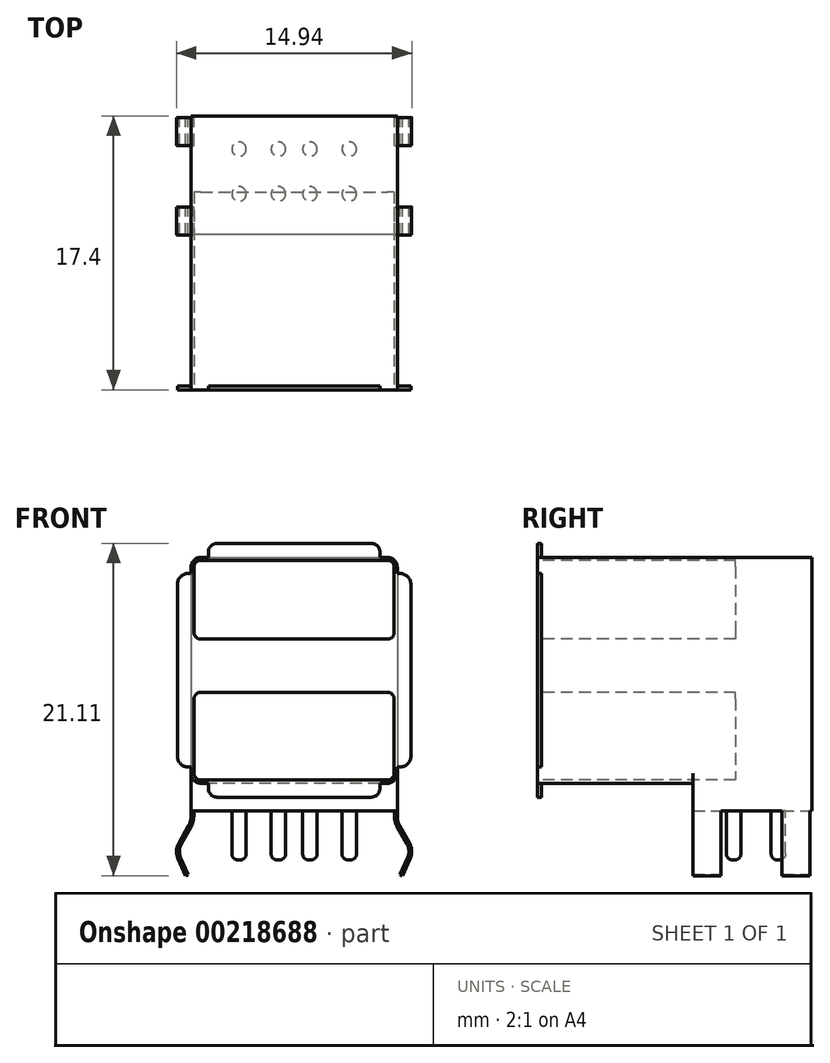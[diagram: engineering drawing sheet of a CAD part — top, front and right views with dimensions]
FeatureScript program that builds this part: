
annotation { "Feature Type Name" : "Feature", "Feature Type Description" : "" }
export const myFeature = defineFeature(function(context is Context, id is Id, definition is map)
    precondition{}
    {
        {
            var Q0;
            Q0=qCreatedBy(makeId("Top.planeOp"),FACE);
            var sketch = newSketch(context, id + "F0", { "sketchPlane" : qUnion([Q0])});
            skLineSegment(sketch, "E0.bottom", {"start": v(-6.55, 8.7) * mm, "end": v(6.55, 8.7) * mm});
            skLineSegment(sketch, "E0.top", {"start": v(-6.55, -8.7) * mm, "end": v(6.55, -8.7) * mm});
            skLineSegment(sketch, "E0.left", {"start": v(-6.55, 8.7) * mm, "end": v(-6.55, -8.7) * mm});
            skLineSegment(sketch, "E0.right", {"start": v(6.55, 8.7) * mm, "end": v(6.55, -8.7) * mm});
            skLineSegment(sketch, "E1", {"start": v(0, 8.7) * mm, "end": v(0, -8.7) * mm, "construction": true});
            skLineSegment(sketch, "E2", {"start": v(-6.55, 0) * mm, "end": v(6.55, 0) * mm, "construction": true});
            skSolve(sketch);
        }
        {
            var Q0;
            Q0 = qSketchRegion(id + "F0", true);
            extrude(context, id + "F1", {"entities" : qUnion([Q0]), "depth" : 14.35 * mm});
        }
        {
            var Q0;
            Q0=makeQuery(id+"F1.opExtrude","CAP_FACE",FACE,{"disambiguationData":[OSD([sQuery(id+"F0.wireOp",EDGE,"E0.bottom"),sQuery(id+"F0.wireOp",EDGE,"E0.top"),sQuery(id+"F0.wireOp",EDGE,"E0.left"),sQuery(id+"F0.wireOp",EDGE,"E0.right")])],"isStart":true});
            var sketch = newSketch(context, id + "F2", { "sketchPlane" : qUnion([Q0])});
            skLineSegment(sketch, "E3.bottom", {"start": v(6.55, -8.7) * mm, "end": v(-6.55, -8.7) * mm});
            skLineSegment(sketch, "E3.top", {"start": v(6.55, -1.16) * mm, "end": v(-6.55, -1.16) * mm});
            skLineSegment(sketch, "E3.left", {"start": v(6.55, -8.7) * mm, "end": v(6.55, -1.16) * mm});
            skLineSegment(sketch, "E3.right", {"start": v(-6.55, -8.7) * mm, "end": v(-6.55, -1.16) * mm});
            skSolve(sketch);
        }
        {
            var Q0;
            Q0 = qSketchRegion(id + "F2", true);
            extrude(context, id + "F3", {"entities" : qUnion([Q0]), "operationType" : NewBodyOperationType.ADD, "depth" : 16.12 * mm - 14.35 * mm});
        }
        {
            var Q0;
            Q0=qCreatedBy(makeId("Front.planeOp"),FACE);
            cPlane(context, id + "F4", {"entities" : qUnion([Q0]), "cplaneType" : CPlaneType.OFFSET, "offset" : 2.03 * mm, "oppositeDirection" : true, "width" : 152.4 * mm, "height" : 152.4 * mm});
        }
        {
            var Q0;
            Q0=qCreatedBy(id+"F4.planeOp",FACE);
            cPlane(context, id + "F5", {"entities" : qUnion([Q0]), "cplaneType" : CPlaneType.OFFSET, "offset" : 5.68 * mm, "oppositeDirection" : true, "width" : 152.4 * mm, "height" : 152.4 * mm});
        }
        {
            var Q0;
            Q0=qCreatedBy(id+"F4.planeOp",FACE);
            var sketch = newSketch(context, id + "F6", { "sketchPlane" : qUnion([Q0])});
            skLineSegment(sketch, "E4", {"start": v(6.55, -1.77) * mm, "end": v(6.55, -2.12) * mm});
            skLineSegment(sketch, "E5", {"start": v(6.7, -2.67) * mm, "end": v(7.32, -3.79) * mm});
            skLineSegment(sketch, "E6", {"start": v(7.37, -4.81) * mm, "end": v(6.88, -5.87) * mm});
            skPoint(sketch, "E7.visualSharp", {"position": v(7.6, -4.29) * mm});
            skArc(sketch, "E7.filletArc", {"start": v(7.37, -4.81) * mm, "mid": v(7.47, -4.3) * mm, "end": v(7.32, -3.79) * mm});
            skPoint(sketch, "E8.visualSharp", {"position": v(6.55, -2.41) * mm});
            skArc(sketch, "E8.filletArc", {"start": v(6.55, -2.12) * mm, "mid": v(6.59, -2.4) * mm, "end": v(6.7, -2.67) * mm});
            skLineSegment(sketch, "E9.0", {"start": v(7.2, -4.74) * mm, "end": v(6.72, -5.8) * mm});
            skLineSegment(sketch, "E9.1", {"start": v(6.37, -1.77) * mm, "end": v(6.37, -2.12) * mm});
            skArc(sketch, "E9.2", {"start": v(6.37, -2.12) * mm, "mid": v(6.41, -2.45) * mm, "end": v(6.54, -2.76) * mm});
            skLineSegment(sketch, "E9.3", {"start": v(6.54, -2.76) * mm, "end": v(7.17, -3.88) * mm});
            skArc(sketch, "E9.4", {"start": v(7.2, -4.74) * mm, "mid": v(7.3, -4.3) * mm, "end": v(7.17, -3.88) * mm});
            skLineSegment(sketch, "E10", {"start": v(6.72, -5.8) * mm, "end": v(6.88, -5.87) * mm});
            skLineSegment(sketch, "E11", {"start": v(6.37, -1.77) * mm, "end": v(6.55, -1.77) * mm});
            skLineSegment(sketch, "E12.MirrorCS", {"start": v(-6.37, -1.77) * mm, "end": v(-6.55, -1.77) * mm});
            skLineSegment(sketch, "E13.MirrorCS", {"start": v(-6.72, -5.8) * mm, "end": v(-6.88, -5.87) * mm});
            skLineSegment(sketch, "E14.MirrorCS", {"start": v(-6.55, -1.77) * mm, "end": v(-6.55, -2.12) * mm});
            skLineSegment(sketch, "E15.MirrorCS", {"start": v(-6.37, -1.77) * mm, "end": v(-6.37, -2.12) * mm});
            skArc(sketch, "E16.MirrorCS", {"start": v(-7.2, -4.74) * mm, "mid": v(-7.3, -4.3) * mm, "end": v(-7.17, -3.88) * mm});
            skLineSegment(sketch, "E17.MirrorCS", {"start": v(-6.54, -2.76) * mm, "end": v(-7.17, -3.88) * mm});
            skArc(sketch, "E18.MirrorCS", {"start": v(-6.37, -2.12) * mm, "mid": v(-6.41, -2.45) * mm, "end": v(-6.54, -2.76) * mm});
            skArc(sketch, "E19.MirrorCS", {"start": v(-7.37, -4.81) * mm, "mid": v(-7.47, -4.3) * mm, "end": v(-7.32, -3.79) * mm});
            skLineSegment(sketch, "E20.MirrorCS", {"start": v(-6.7, -2.67) * mm, "end": v(-7.32, -3.79) * mm});
            skArc(sketch, "E21.MirrorCS", {"start": v(-6.55, -2.12) * mm, "mid": v(-6.59, -2.4) * mm, "end": v(-6.7, -2.67) * mm});
            skPoint(sketch, "E22.MirrorP", {"position": v(-7.6, -4.29) * mm});
            skPoint(sketch, "E23.MirrorP", {"position": v(-6.55, -2.41) * mm});
            skLineSegment(sketch, "E24.MirrorCS", {"start": v(-7.37, -4.81) * mm, "end": v(-6.88, -5.87) * mm});
            skLineSegment(sketch, "E25.MirrorCS", {"start": v(-7.2, -4.74) * mm, "end": v(-6.72, -5.8) * mm});
            skSolve(sketch);
        }
        {
            var Q0;
            Q0 = qSketchRegion(id + "F6", true);
            extrude(context, id + "F7", {"entities" : qUnion([Q0]), "operationType" : NewBodyOperationType.ADD, "endBound" : BoundingType.SYMMETRIC, "depth" : 1.78 * mm});
        }
        {
            var Q0;
            Q0=qCreatedBy(id+"F5.planeOp",FACE);
            var sketch = newSketch(context, id + "F8", { "sketchPlane" : qUnion([Q0])});
            skLineSegment(sketch, "E26.0", {"start": v(6.37, -1.77) * mm, "end": v(6.37, -2.12) * mm});
            skLineSegment(sketch, "E26.1", {"start": v(6.55, -1.77) * mm, "end": v(6.55, -2.12) * mm});
            skArc(sketch, "E26.2", {"start": v(6.37, -2.12) * mm, "mid": v(6.41, -2.45) * mm, "end": v(6.54, -2.76) * mm});
            skArc(sketch, "E26.3", {"start": v(6.55, -2.12) * mm, "mid": v(6.59, -2.4) * mm, "end": v(6.7, -2.67) * mm});
            skLineSegment(sketch, "E26.4", {"start": v(6.54, -2.76) * mm, "end": v(7.17, -3.88) * mm});
            skLineSegment(sketch, "E26.5", {"start": v(6.7, -2.67) * mm, "end": v(7.32, -3.79) * mm});
            skArc(sketch, "E26.6", {"start": v(7.2, -4.74) * mm, "mid": v(7.3, -4.3) * mm, "end": v(7.17, -3.88) * mm});
            skArc(sketch, "E26.7", {"start": v(7.37, -4.81) * mm, "mid": v(7.47, -4.3) * mm, "end": v(7.32, -3.79) * mm});
            skLineSegment(sketch, "E26.8", {"start": v(6.72, -5.8) * mm, "end": v(6.88, -5.87) * mm});
            skLineSegment(sketch, "E26.9", {"start": v(7.2, -4.74) * mm, "end": v(6.72, -5.8) * mm});
            skLineSegment(sketch, "E26.10", {"start": v(7.37, -4.81) * mm, "end": v(6.88, -5.87) * mm});
            skLineSegment(sketch, "E26.11", {"start": v(-7.37, -4.81) * mm, "end": v(-6.88, -5.87) * mm});
            skArc(sketch, "E26.12", {"start": v(-7.37, -4.81) * mm, "mid": v(-7.47, -4.3) * mm, "end": v(-7.32, -3.79) * mm});
            skLineSegment(sketch, "E26.13", {"start": v(-6.7, -2.67) * mm, "end": v(-7.32, -3.79) * mm});
            skArc(sketch, "E26.14", {"start": v(-6.55, -2.12) * mm, "mid": v(-6.59, -2.4) * mm, "end": v(-6.7, -2.67) * mm});
            skLineSegment(sketch, "E26.15", {"start": v(-6.55, -1.77) * mm, "end": v(-6.55, -2.12) * mm});
            skLineSegment(sketch, "E26.16", {"start": v(-6.37, -1.77) * mm, "end": v(-6.37, -2.12) * mm});
            skArc(sketch, "E26.17", {"start": v(-6.37, -2.12) * mm, "mid": v(-6.41, -2.45) * mm, "end": v(-6.54, -2.76) * mm});
            skLineSegment(sketch, "E26.18", {"start": v(-6.54, -2.76) * mm, "end": v(-7.17, -3.88) * mm});
            skArc(sketch, "E26.19", {"start": v(-7.2, -4.74) * mm, "mid": v(-7.3, -4.3) * mm, "end": v(-7.17, -3.88) * mm});
            skLineSegment(sketch, "E26.20", {"start": v(-7.2, -4.74) * mm, "end": v(-6.72, -5.8) * mm});
            skLineSegment(sketch, "E26.21", {"start": v(-6.72, -5.8) * mm, "end": v(-6.88, -5.87) * mm});
            skLineSegment(sketch, "E27", {"start": v(-6.55, -1.77) * mm, "end": v(-6.37, -1.77) * mm});
            skLineSegment(sketch, "E28", {"start": v(6.37, -1.77) * mm, "end": v(6.55, -1.77) * mm});
            skSolve(sketch);
        }
        {
            var Q0;
            Q0=makeQuery(id+"F8.imprint","IMPRINT",FACE,{"disambiguationData":[TD([[makeQuery(id+"F8.imprint","IMPRINT",EDGE,{"derivedFrom":sQuery(id+"F8.wireOp",EDGE,"E26.11")}),1.0]])]});
            var Q1;
            Q1=makeQuery(id+"F8.imprint","IMPRINT",FACE,{"disambiguationData":[TD([[makeQuery(id+"F8.imprint","IMPRINT",EDGE,{"derivedFrom":sQuery(id+"F8.wireOp",EDGE,"E26.0")}),1.0]])]});
            extrude(context, id + "F9", {"entities" : qUnion([Q0, Q1]), "operationType" : NewBodyOperationType.ADD, "endBound" : BoundingType.SYMMETRIC, "depth" : 1.78 * mm});
        }
        {
            var Q0;
            Q0=makeQuery(id+"F3.opExtrude","CAP_FACE",FACE,{"disambiguationData":[OSD([sQuery(id+"F2.wireOp",EDGE,"E3.bottom"),sQuery(id+"F2.wireOp",EDGE,"E3.top"),sQuery(id+"F2.wireOp",EDGE,"E3.left"),sQuery(id+"F2.wireOp",EDGE,"E3.right")])],"isStart":false});
            var sketch = newSketch(context, id + "F10", { "sketchPlane" : qUnion([Q0])});
            skCircle(sketch, "E29", {"center": v(3.5, -6.59) * mm, "radius": 0.46 * mm});
            skCircle(sketch, "E30", {"center": v(1, -6.59) * mm, "radius": 0.46 * mm});
            skCircle(sketch, "E31", {"center": v(-1, -6.59) * mm, "radius": 0.46 * mm});
            skCircle(sketch, "E32", {"center": v(-3.5, -6.59) * mm, "radius": 0.46 * mm});
            skCircle(sketch, "E33", {"center": v(3.5, -3.74) * mm, "radius": 0.46 * mm});
            skCircle(sketch, "E34", {"center": v(1, -3.74) * mm, "radius": 0.46 * mm});
            skCircle(sketch, "E35", {"center": v(-1, -3.74) * mm, "radius": 0.46 * mm});
            skCircle(sketch, "E36", {"center": v(-3.5, -3.74) * mm, "radius": 0.46 * mm});
            skSolve(sketch);
        }
        {
            var Q0;
            Q0 = qSketchRegion(id + "F10", true);
            extrude(context, id + "F11", {"entities" : qUnion([Q0]), "operationType" : NewBodyOperationType.ADD, "depth" : 3.1 * mm});
        }
        {
            var Q0;
            Q0=makeQuery(id+"F11.opExtrude","CAP_EDGE",EDGE,{"disambiguationData":[OSD([sQuery(id+"F10.wireOp",EDGE,"E29")])],"isStart":false});
            var Q1;
            Q1=makeQuery(id+"F11.opExtrude","CAP_EDGE",EDGE,{"disambiguationData":[OSD([sQuery(id+"F10.wireOp",EDGE,"E30")])],"isStart":false});
            var Q2;
            Q2=makeQuery(id+"F11.opExtrude","CAP_EDGE",EDGE,{"disambiguationData":[OSD([sQuery(id+"F10.wireOp",EDGE,"E31")])],"isStart":false});
            var Q3;
            Q3=makeQuery(id+"F11.opExtrude","CAP_EDGE",EDGE,{"disambiguationData":[OSD([sQuery(id+"F10.wireOp",EDGE,"E32")])],"isStart":false});
            var Q4;
            Q4=makeQuery(id+"F11.opExtrude","CAP_EDGE",EDGE,{"disambiguationData":[OSD([sQuery(id+"F10.wireOp",EDGE,"E33")])],"isStart":false});
            var Q5;
            Q5=makeQuery(id+"F11.opExtrude","CAP_EDGE",EDGE,{"disambiguationData":[OSD([sQuery(id+"F10.wireOp",EDGE,"E34")])],"isStart":false});
            var Q6;
            Q6=makeQuery(id+"F11.opExtrude","CAP_EDGE",EDGE,{"disambiguationData":[OSD([sQuery(id+"F10.wireOp",EDGE,"E35")])],"isStart":false});
            var Q7;
            Q7=makeQuery(id+"F11.opExtrude","CAP_EDGE",EDGE,{"disambiguationData":[OSD([sQuery(id+"F10.wireOp",EDGE,"E36")])],"isStart":false});
            fillet(context, id + "F12", {"entities" : qUnion([Q0, Q1, Q2, Q3, Q4, Q5, Q6, Q7]), "radius" : 0.38 * mm, "tangentPropagation" : true, "allowEdgeOverflow" : false});
        }
        {
            var Q0;
            Q0=makeQuery(id+"F1.opExtrude","SWEPT_FACE",FACE,{"disambiguationData":[OSD([sQuery(id+"F0.wireOp",EDGE,"E0.top")])]});
            var sketch = newSketch(context, id + "F13", { "sketchPlane" : qUnion([Q0])});
            skLineSegment(sketch, "E37.bottom", {"start": v(-4.9, 15.24) * mm, "end": v(4.9, 15.24) * mm});
            skLineSegment(sketch, "E37.top", {"start": v(-4.9, -0.89) * mm, "end": v(4.9, -0.89) * mm});
            skLineSegment(sketch, "E37.left", {"start": v(-5.45, 14.7) * mm, "end": v(-5.45, -0.34) * mm});
            skLineSegment(sketch, "E37.right", {"start": v(5.45, 14.7) * mm, "end": v(5.45, -0.34) * mm});
            skLineSegment(sketch, "E38", {"start": v(0, 15.24) * mm, "end": v(0, -0.89) * mm, "construction": true});
            skLineSegment(sketch, "E39", {"start": v(-5.45, 7.17) * mm, "end": v(5.45, 7.17) * mm, "construction": true});
            skLineSegment(sketch, "E40", {"start": v(-6.55, 7.17) * mm, "end": v(6.55, 7.17) * mm, "construction": true});
            skPoint(sketch, "E41.visualSharp", {"position": v(-5.45, 15.24) * mm});
            skArc(sketch, "E41.filletArc", {"start": v(-4.9, 15.24) * mm, "mid": v(-5.29, 15.08) * mm, "end": v(-5.45, 14.7) * mm});
            skPoint(sketch, "E42.visualSharp", {"position": v(5.45, 15.24) * mm});
            skArc(sketch, "E42.filletArc", {"start": v(5.45, 14.7) * mm, "mid": v(5.29, 15.08) * mm, "end": v(4.9, 15.24) * mm});
            skPoint(sketch, "E43.visualSharp", {"position": v(-5.45, -0.89) * mm});
            skArc(sketch, "E43.filletArc", {"start": v(-5.45, -0.34) * mm, "mid": v(-5.29, -0.73) * mm, "end": v(-4.9, -0.89) * mm});
            skPoint(sketch, "E44.visualSharp", {"position": v(5.45, -0.89) * mm});
            skArc(sketch, "E44.filletArc", {"start": v(4.9, -0.89) * mm, "mid": v(5.29, -0.73) * mm, "end": v(5.45, -0.34) * mm});
            skSolve(sketch);
        }
        {
            var Q0;
            Q0 = qSketchRegion(id + "F13", true);
            extrude(context, id + "F14", {"entities" : qUnion([Q0]), "operationType" : NewBodyOperationType.ADD, "oppositeDirection" : true, "depth" : 0.25 * mm});
        }
        {
            var Q0;
            Q0=makeQuery(id+"F14.boolean.opBoolean","MERGE",FACE,{"derivedFrom":[makeQuery(id+"F1.opExtrude","SWEPT_FACE",FACE,{"disambiguationData":[OSD([sQuery(id+"F0.wireOp",EDGE,"E0.top")])]}),makeQuery(id+"F14.opExtrude","CAP_FACE",FACE,{"disambiguationData":[OSD([sQuery(id+"F13.wireOp",EDGE,"E37.bottom"),sQuery(id+"F13.wireOp",EDGE,"E37.top"),sQuery(id+"F13.wireOp",EDGE,"E37.left"),sQuery(id+"F13.wireOp",EDGE,"E37.right"),sQuery(id+"F13.wireOp",EDGE,"E41.filletArc"),sQuery(id+"F13.wireOp",EDGE,"E42.filletArc"),sQuery(id+"F13.wireOp",EDGE,"E43.filletArc"),sQuery(id+"F13.wireOp",EDGE,"E44.filletArc")])],"isStart":true})]});
            var sketch = newSketch(context, id + "F15", { "sketchPlane" : qUnion([Q0])});
            skLineSegment(sketch, "E45.bottom", {"start": v(-6.72, 13.32) * mm, "end": v(6.72, 13.32) * mm});
            skLineSegment(sketch, "E45.top", {"start": v(-6.72, 1.02) * mm, "end": v(6.72, 1.02) * mm});
            skLineSegment(sketch, "E45.left", {"start": v(-7.42, 12.62) * mm, "end": v(-7.42, 1.73) * mm});
            skLineSegment(sketch, "E45.right", {"start": v(7.42, 12.62) * mm, "end": v(7.42, 1.73) * mm});
            skLineSegment(sketch, "E46", {"start": v(-7.42, 7.17) * mm, "end": v(7.42, 7.17) * mm, "construction": true});
            skLineSegment(sketch, "E47", {"start": v(-6.55, 7.17) * mm, "end": v(6.55, 7.17) * mm, "construction": true});
            skLineSegment(sketch, "E48", {"start": v(0, 13.32) * mm, "end": v(0, 1.02) * mm, "construction": true});
            skPoint(sketch, "E49.visualSharp", {"position": v(-7.42, 13.32) * mm});
            skArc(sketch, "E49.filletArc", {"start": v(-6.72, 13.33) * mm, "mid": v(-7.21, 13.12) * mm, "end": v(-7.42, 12.62) * mm});
            skPoint(sketch, "E50.visualSharp", {"position": v(-7.42, 1.02) * mm});
            skArc(sketch, "E50.filletArc", {"start": v(-7.42, 1.73) * mm, "mid": v(-7.21, 1.23) * mm, "end": v(-6.72, 1.02) * mm});
            skPoint(sketch, "E51.visualSharp", {"position": v(7.42, 13.32) * mm});
            skArc(sketch, "E51.filletArc", {"start": v(7.42, 12.62) * mm, "mid": v(7.21, 13.12) * mm, "end": v(6.72, 13.33) * mm});
            skPoint(sketch, "E52.visualSharp", {"position": v(7.42, 1.02) * mm});
            skArc(sketch, "E52.filletArc", {"start": v(6.72, 1.02) * mm, "mid": v(7.21, 1.23) * mm, "end": v(7.42, 1.73) * mm});
            skSolve(sketch);
        }
        {
            var Q0;
            Q0 = qSketchRegion(id + "F15", true);
            extrude(context, id + "F16", {"entities" : qUnion([Q0]), "operationType" : NewBodyOperationType.ADD, "oppositeDirection" : true, "depth" : 0.25 * mm});
        }
        {
            var Q0;
            Q0=makeQuery(id+"F1.opExtrude","CAP_EDGE",EDGE,{"disambiguationData":[OSD([sQuery(id+"F0.wireOp",EDGE,"E0.left")])],"isStart":false});
            var Q1;
            Q1=makeQuery(id+"F1.opExtrude","CAP_EDGE",EDGE,{"disambiguationData":[OSD([sQuery(id+"F0.wireOp",EDGE,"E0.right")])],"isStart":false});
            var Q2;
            Q2=makeQuery(id+"F1.opExtrude","CAP_EDGE",EDGE,{"disambiguationData":[OSD([sQuery(id+"F0.wireOp",EDGE,"E0.left")])],"isStart":true});
            var Q3;
            Q3=makeQuery(id+"F1.opExtrude","CAP_EDGE",EDGE,{"disambiguationData":[OSD([sQuery(id+"F0.wireOp",EDGE,"E0.right")])],"isStart":true});
            fillet(context, id + "F17", {"entities" : qUnion([Q0, Q1, Q2, Q3]), "radius" : 0.64 * mm, "tangentPropagation" : true, "allowEdgeOverflow" : false});
        }
        {
            var Q0;
            Q0=makeQuery(id+"F16.boolean.opBoolean","MERGE",FACE,{"derivedFrom":[makeQuery(id+"F14.boolean.opBoolean","MERGE",FACE,{"derivedFrom":[makeQuery(id+"F1.opExtrude","SWEPT_FACE",FACE,{"disambiguationData":[OSD([sQuery(id+"F0.wireOp",EDGE,"E0.top")])]}),makeQuery(id+"F14.opExtrude","CAP_FACE",FACE,{"disambiguationData":[OSD([sQuery(id+"F13.wireOp",EDGE,"E37.bottom"),sQuery(id+"F13.wireOp",EDGE,"E37.top"),sQuery(id+"F13.wireOp",EDGE,"E37.left"),sQuery(id+"F13.wireOp",EDGE,"E37.right"),sQuery(id+"F13.wireOp",EDGE,"E41.filletArc"),sQuery(id+"F13.wireOp",EDGE,"E42.filletArc"),sQuery(id+"F13.wireOp",EDGE,"E43.filletArc"),sQuery(id+"F13.wireOp",EDGE,"E44.filletArc")])],"isStart":true})]}),makeQuery(id+"F16.opExtrude","CAP_FACE",FACE,{"disambiguationData":[OSD([sQuery(id+"F15.wireOp",EDGE,"E45.bottom"),sQuery(id+"F15.wireOp",EDGE,"E45.top"),sQuery(id+"F15.wireOp",EDGE,"E45.left"),sQuery(id+"F15.wireOp",EDGE,"E45.right"),sQuery(id+"F15.wireOp",EDGE,"E49.filletArc"),sQuery(id+"F15.wireOp",EDGE,"E50.filletArc"),sQuery(id+"F15.wireOp",EDGE,"E51.filletArc"),sQuery(id+"F15.wireOp",EDGE,"E52.filletArc")])],"isStart":true})]});
            var sketch = newSketch(context, id + "F18", { "sketchPlane" : qUnion([Q0])});
            skLineSegment(sketch, "E53.bottom", {"start": v(-5.94, 14.16) * mm, "end": v(5.94, 14.16) * mm});
            skLineSegment(sketch, "E53.top", {"start": v(-5.94, 9.16) * mm, "end": v(5.94, 9.16) * mm});
            skLineSegment(sketch, "E53.left", {"start": v(-6.35, 13.75) * mm, "end": v(-6.35, 9.56) * mm});
            skLineSegment(sketch, "E53.right", {"start": v(6.35, 13.75) * mm, "end": v(6.35, 9.56) * mm});
            skLineSegment(sketch, "E54.bottom", {"start": v(-5.94, 5.77) * mm, "end": v(5.94, 5.77) * mm});
            skLineSegment(sketch, "E54.top", {"start": v(-5.94, 0.2) * mm, "end": v(5.94, 0.2) * mm});
            skLineSegment(sketch, "E54.left", {"start": v(-6.35, 5.36) * mm, "end": v(-6.35, 0.61) * mm});
            skLineSegment(sketch, "E54.right", {"start": v(6.35, 5.36) * mm, "end": v(6.35, 0.61) * mm});
            skLineSegment(sketch, "E55", {"start": v(0, 14.16) * mm, "end": v(0, 9.16) * mm, "construction": true});
            skLineSegment(sketch, "E56", {"start": v(0, 5.77) * mm, "end": v(0, 0.2) * mm, "construction": true});
            skPoint(sketch, "E57.visualSharp", {"position": v(-6.35, 14.16) * mm});
            skArc(sketch, "E57.filletArc", {"start": v(-5.94, 14.16) * mm, "mid": v(-6.23, 14.04) * mm, "end": v(-6.35, 13.75) * mm});
            skPoint(sketch, "E58.visualSharp", {"position": v(6.35, 14.16) * mm});
            skArc(sketch, "E58.filletArc", {"start": v(6.35, 13.75) * mm, "mid": v(6.23, 14.04) * mm, "end": v(5.94, 14.16) * mm});
            skPoint(sketch, "E59.visualSharp", {"position": v(6.35, 9.16) * mm});
            skArc(sketch, "E59.filletArc", {"start": v(5.94, 9.16) * mm, "mid": v(6.23, 9.28) * mm, "end": v(6.35, 9.56) * mm});
            skPoint(sketch, "E60.visualSharp", {"position": v(-6.35, 9.16) * mm});
            skArc(sketch, "E60.filletArc", {"start": v(-6.35, 9.56) * mm, "mid": v(-6.23, 9.28) * mm, "end": v(-5.94, 9.16) * mm});
            skPoint(sketch, "E61.visualSharp", {"position": v(-6.35, 5.77) * mm});
            skArc(sketch, "E61.filletArc", {"start": v(-5.94, 5.77) * mm, "mid": v(-6.23, 5.65) * mm, "end": v(-6.35, 5.36) * mm});
            skPoint(sketch, "E62.visualSharp", {"position": v(6.35, 5.77) * mm});
            skArc(sketch, "E62.filletArc", {"start": v(6.35, 5.36) * mm, "mid": v(6.23, 5.65) * mm, "end": v(5.94, 5.77) * mm});
            skPoint(sketch, "E63.visualSharp", {"position": v(6.35, 0.2) * mm});
            skArc(sketch, "E63.filletArc", {"start": v(5.94, 0.2) * mm, "mid": v(6.23, 0.33) * mm, "end": v(6.35, 0.61) * mm});
            skPoint(sketch, "E64.visualSharp", {"position": v(-6.35, 0.2) * mm});
            skArc(sketch, "E64.filletArc", {"start": v(-6.35, 0.61) * mm, "mid": v(-6.23, 0.33) * mm, "end": v(-5.94, 0.2) * mm});
            skSolve(sketch);
        }
        {
            var Q0;
            Q0 = qSketchRegion(id + "F18", true);
            extrude(context, id + "F19", {"entities" : qUnion([Q0]), "operationType" : NewBodyOperationType.REMOVE, "oppositeDirection" : true, "depth" : 12.57 * mm});
        }
    });
